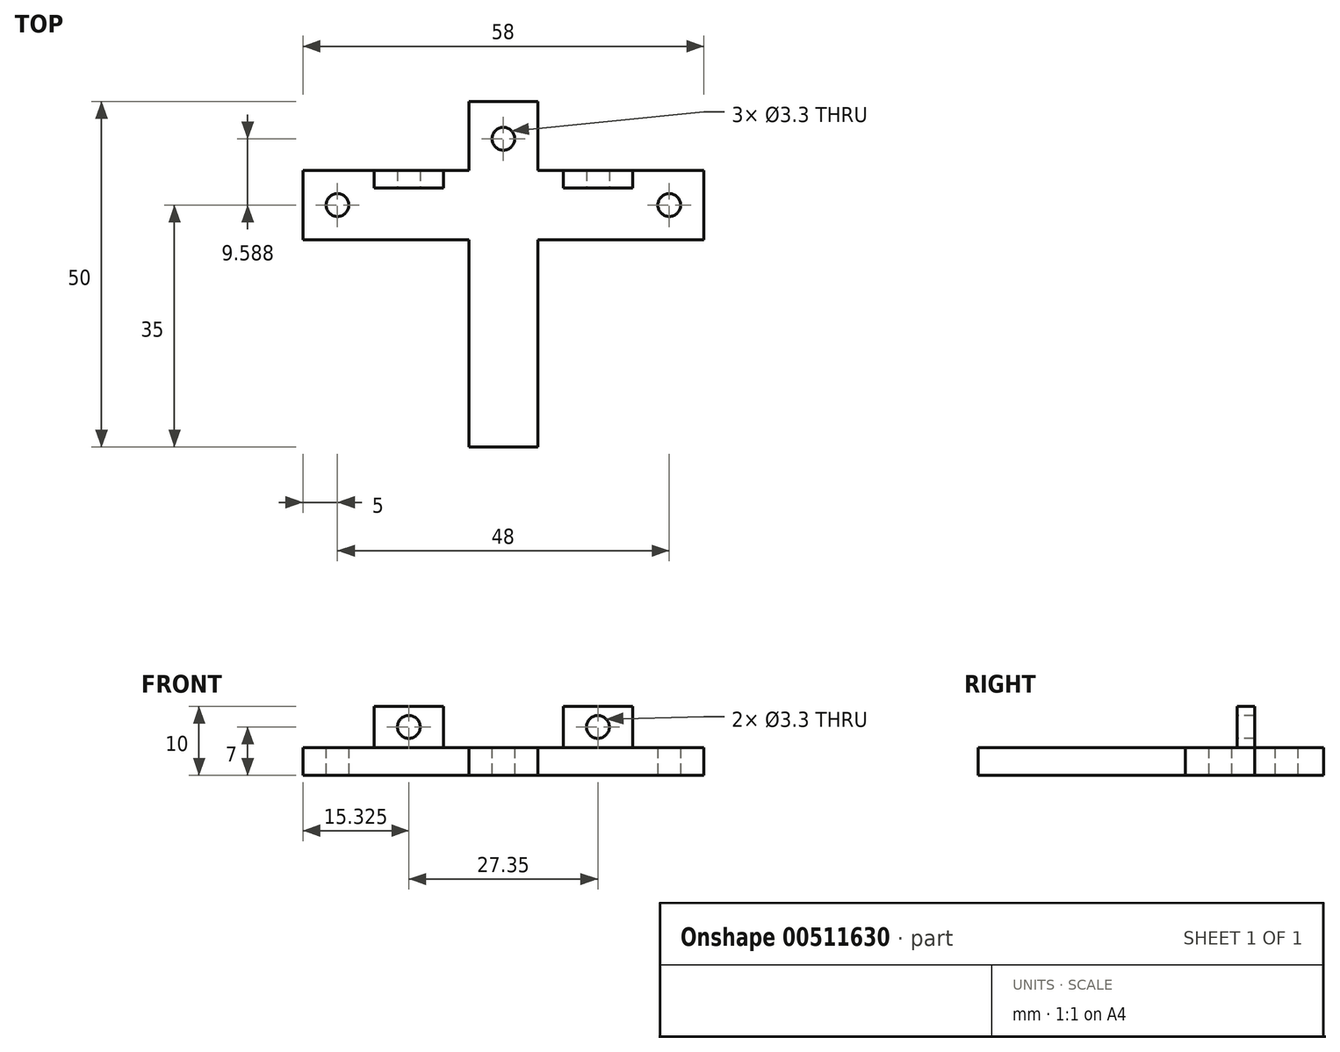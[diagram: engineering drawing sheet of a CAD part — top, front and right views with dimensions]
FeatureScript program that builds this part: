
annotation { "Feature Type Name" : "Feature", "Feature Type Description" : "" }
export const myFeature = defineFeature(function(context is Context, id is Id, definition is map)
    precondition{}
    {
        {
            var Q0;
            Q0=qCreatedBy(makeId("Top.planeOp"),FACE);
            var sketch = newSketch(context, id + "F0", { "sketchPlane" : qUnion([Q0])});
            skLineSegment(sketch, "E0.bottom", {"start": v(0, 0) * mm, "end": v(10, 0) * mm});
            skLineSegment(sketch, "E0.top", {"start": v(0, -50) * mm, "end": v(10, -50) * mm});
            skLineSegment(sketch, "E0.left", {"start": v(0, 0) * mm, "end": v(0, -10) * mm});
            skLineSegment(sketch, "E0.right", {"start": v(10, 0) * mm, "end": v(10, -10) * mm});
            skLineSegment(sketch, "E1.bottom", {"start": v(34, -20) * mm, "end": v(10, -20) * mm});
            skLineSegment(sketch, "E1.top", {"start": v(34, -10) * mm, "end": v(10, -10) * mm});
            skLineSegment(sketch, "E1.left", {"start": v(34, -20) * mm, "end": v(34, -10) * mm});
            skLineSegment(sketch, "E1.right", {"start": v(-24, -20) * mm, "end": v(-24, -10) * mm});
            skLineSegment(sketch, "E2.trimOffspring", {"start": v(0, -20) * mm, "end": v(0, -50) * mm});
            skLineSegment(sketch, "E3.trimOffspring", {"start": v(0, -20) * mm, "end": v(-24, -20) * mm});
            skLineSegment(sketch, "E4.trimOffspring", {"start": v(10, -20) * mm, "end": v(10, -50) * mm});
            skLineSegment(sketch, "E5.trimOffspring", {"start": v(0, -10) * mm, "end": v(-24, -10) * mm});
            skCircle(sketch, "E6", {"center": v(-19, -15) * mm, "radius": 1.65 * mm});
            skCircle(sketch, "E7", {"center": v(5, -5.41) * mm, "radius": 1.65 * mm});
            skCircle(sketch, "E8", {"center": v(29, -15) * mm, "radius": 1.65 * mm});
            skLineSegment(sketch, "E9", {"start": v(-24, -15) * mm, "end": v(34, -15) * mm, "construction": true});
            skLineSegment(sketch, "E10", {"start": v(5, 0) * mm, "end": v(5, -50) * mm, "construction": true});
            skSolve(sketch);
        }
        {
            var Q0;
            Q0 = qSketchRegion(id + "F0", true);
            extrude(context, id + "F1", {"entities" : qUnion([Q0]), "depth" : 4 * mm, "offsetDistance" : 25 * mm});
        }
        {
            var Q0;
            Q0=makeQuery(id+"F1.opExtrude","CAP_FACE",FACE,{"disambiguationData":[OSD([sQuery(id+"F0.wireOp",EDGE,"E0.bottom"),sQuery(id+"F0.wireOp",EDGE,"E0.top"),sQuery(id+"F0.wireOp",EDGE,"E0.left"),sQuery(id+"F0.wireOp",EDGE,"E0.right"),sQuery(id+"F0.wireOp",EDGE,"E1.bottom"),sQuery(id+"F0.wireOp",EDGE,"E1.top"),sQuery(id+"F0.wireOp",EDGE,"E1.left"),sQuery(id+"F0.wireOp",EDGE,"E1.right"),sQuery(id+"F0.wireOp",EDGE,"E2.trimOffspring"),sQuery(id+"F0.wireOp",EDGE,"E3.trimOffspring"),sQuery(id+"F0.wireOp",EDGE,"E4.trimOffspring"),sQuery(id+"F0.wireOp",EDGE,"E5.trimOffspring"),sQuery(id+"F0.wireOp",EDGE,"E6"),sQuery(id+"F0.wireOp",EDGE,"E7"),sQuery(id+"F0.wireOp",EDGE,"E8")])],"isStart":false});
            var sketch = newSketch(context, id + "F2", { "sketchPlane" : qUnion([Q0])});
            skLineSegment(sketch, "E11", {"start": v(-24, -15) * mm, "end": v(34, -15) * mm, "construction": true});
            skLineSegment(sketch, "E12", {"start": v(0, -10) * mm, "end": v(0, -20) * mm, "construction": true});
            skLineSegment(sketch, "E13", {"start": v(-17.35, -15) * mm, "end": v(0, -15) * mm, "construction": true});
            skLineSegment(sketch, "E14", {"start": v(-8.67, -15) * mm, "end": v(-8.67, -10) * mm, "construction": true});
            skLineSegment(sketch, "E15.bottom", {"start": v(-13.67, -10) * mm, "end": v(-3.68, -10) * mm});
            skLineSegment(sketch, "E15.top", {"start": v(-13.67, -12.5) * mm, "end": v(-3.68, -12.5) * mm});
            skLineSegment(sketch, "E15.left", {"start": v(-13.68, -10) * mm, "end": v(-13.68, -12.5) * mm});
            skLineSegment(sketch, "E15.right", {"start": v(-3.67, -10) * mm, "end": v(-3.68, -12.5) * mm});
            skSolve(sketch);
        }
        {
            var Q0;
            Q0 = qSketchRegion(id + "F2", true);
            extrude(context, id + "F3", {"entities" : qUnion([Q0]), "operationType" : NewBodyOperationType.ADD, "depth" : 6 * mm, "offsetDistance" : 25 * mm});
        }
        {
            var Q0;
            Q0=makeQuery(id+"F3.opExtrude","SWEPT_FACE",FACE,{"disambiguationData":[OSD([sQuery(id+"F2.wireOp",EDGE,"E15.top")])]});
            var sketch = newSketch(context, id + "F4", { "sketchPlane" : qUnion([Q0])});
            skCircle(sketch, "E16", {"center": v(-8.67, 7) * mm, "radius": 1.65 * mm});
            skSolve(sketch);
        }
        {
            var Q0;
            Q0=makeQuery(id+"F4.imprint","IMPRINT",FACE,{"disambiguationData":[TD([[makeQuery(id+"F4.imprint","IMPRINT",EDGE,{"derivedFrom":sQuery(id+"F4.wireOp",EDGE,"E16")}),1.0]])]});
            extrude(context, id + "F5", {"entities" : qUnion([Q0]), "operationType" : NewBodyOperationType.REMOVE, "endBound" : BoundingType.THROUGH_ALL, "oppositeDirection" : true, "depth" : 25 * mm, "offsetDistance" : 25 * mm});
        }
        {
            var Q0;
            Q0=makeQuery(id+"F1.opExtrude","SWEPT_FACE",FACE,{"disambiguationData":[OSD([sQuery(id+"F0.wireOp",EDGE,"E4.trimOffspring")])]});
            cPlane(context, id + "F6", {"entities" : qUnion([Q0]), "cplaneType" : CPlaneType.OFFSET, "offset" : 5 * mm, "oppositeDirection" : true, "width" : 150 * mm, "height" : 150 * mm});
        }
        {
            var Q0;
            Q0=makeQuery(id+"F1.opExtrude","SWEPT_BODY",BODY,{"disambiguationData":[OSD([sQuery(id+"F0.wireOp",EDGE,"E0.bottom"),sQuery(id+"F0.wireOp",EDGE,"E0.top"),sQuery(id+"F0.wireOp",EDGE,"E0.left"),sQuery(id+"F0.wireOp",EDGE,"E0.right"),sQuery(id+"F0.wireOp",EDGE,"E1.bottom"),sQuery(id+"F0.wireOp",EDGE,"E1.top"),sQuery(id+"F0.wireOp",EDGE,"E1.left"),sQuery(id+"F0.wireOp",EDGE,"E1.right"),sQuery(id+"F0.wireOp",EDGE,"E2.trimOffspring"),sQuery(id+"F0.wireOp",EDGE,"E3.trimOffspring"),sQuery(id+"F0.wireOp",EDGE,"E4.trimOffspring"),sQuery(id+"F0.wireOp",EDGE,"E5.trimOffspring"),sQuery(id+"F0.wireOp",EDGE,"E6"),sQuery(id+"F0.wireOp",EDGE,"E7"),sQuery(id+"F0.wireOp",EDGE,"E8")])]});
            var Q1;
            Q1=qCreatedBy(id+"F6.planeOp",FACE);
            mirror(context, id + "F7", {"operationType" : NewBodyOperationType.ADD, "entities" : qUnion([Q0]), "mirrorPlane" : qUnion([Q1])});
        }
    });
